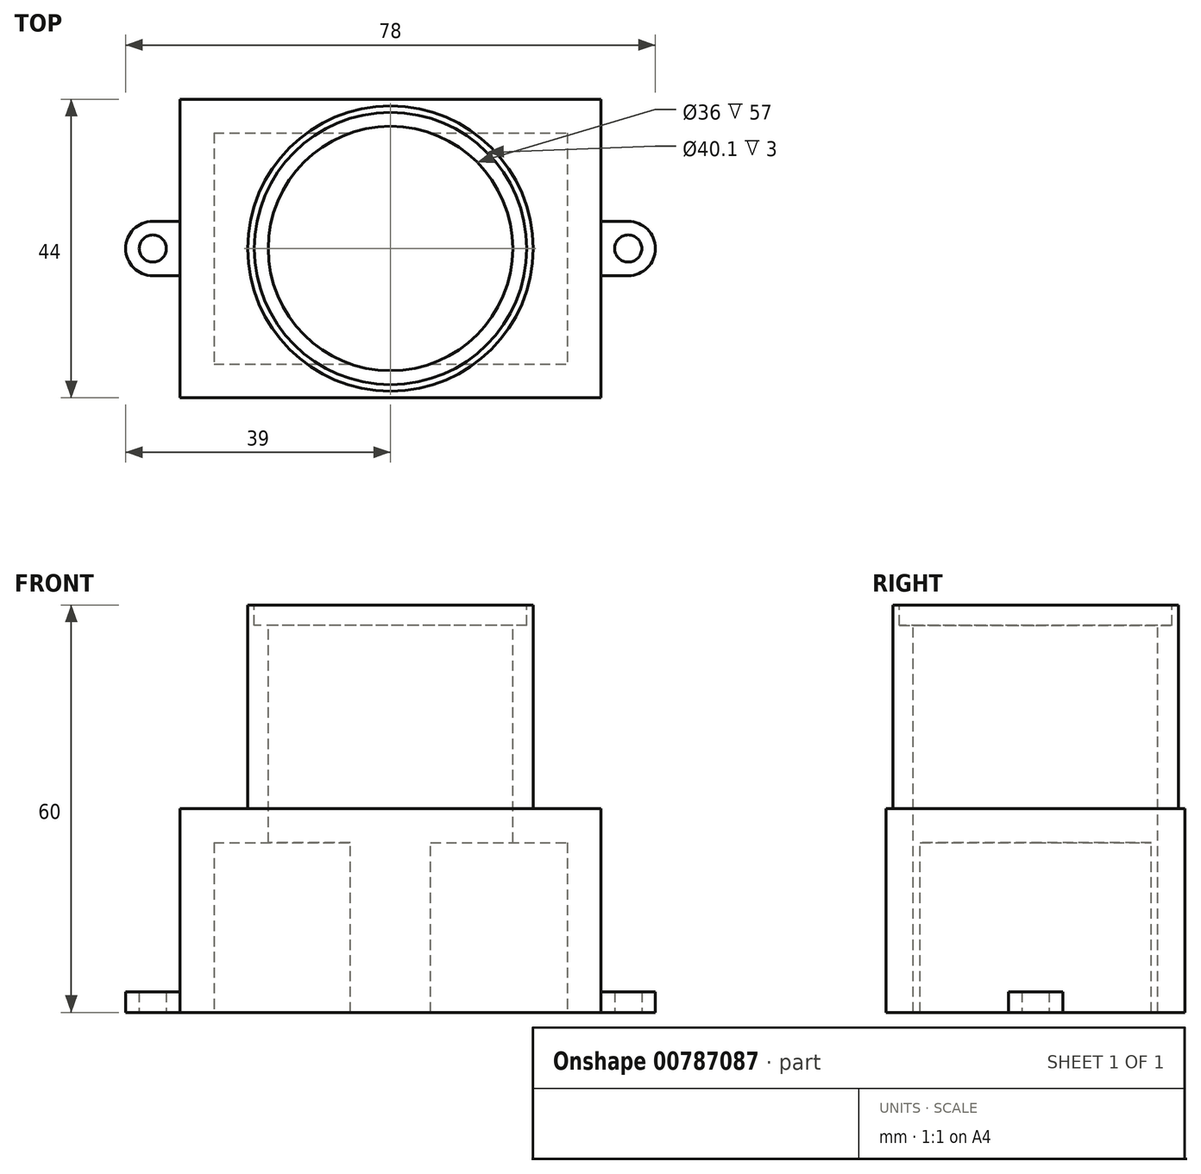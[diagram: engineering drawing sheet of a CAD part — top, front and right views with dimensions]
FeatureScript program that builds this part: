
annotation { "Feature Type Name" : "Feature", "Feature Type Description" : "" }
export const myFeature = defineFeature(function(context is Context, id is Id, definition is map)
    precondition{}
    {
        {
            var Q0;
            Q0=qCreatedBy(makeId("Top.planeOp"),FACE);
            var sketch = newSketch(context, id + "F0", { "sketchPlane" : qUnion([Q0])});
            skLineSegment(sketch, "E0.bottom", {"start": v(-31, 22) * mm, "end": v(31, 22) * mm});
            skLineSegment(sketch, "E0.top", {"start": v(-31, -22) * mm, "end": v(31, -22) * mm});
            skLineSegment(sketch, "E0.left", {"start": v(-31, 22) * mm, "end": v(-31, -22) * mm});
            skLineSegment(sketch, "E0.right", {"start": v(31, 22) * mm, "end": v(31, -22) * mm});
            skPoint(sketch, "E0.middle", {"position": v(0, 0) * mm});
            skSolve(sketch);
        }
        {
            var Q0;
            Q0=makeQuery(id+"F0.imprint","IMPRINT",FACE,{"disambiguationData":[TD([[makeQuery(id+"F0.imprint","IMPRINT",EDGE,{"derivedFrom":sQuery(id+"F0.wireOp",EDGE,"E0.bottom")}),-1.0]])]});
            extrude(context, id + "F1", {"entities" : qUnion([Q0]), "depth" : 30 * mm, "hasSecondDirection" : true, "secondDirectionOppositeDirection" : true, "secondDirectionDepth" : 30 * mm});
        }
        {
            var Q0;
            Q0=makeQuery(id+"F1.opExtrude","CAP_FACE",FACE,{"disambiguationData":[OSD([sQuery(id+"F0.wireOp",EDGE,"E0.bottom"),sQuery(id+"F0.wireOp",EDGE,"E0.top"),sQuery(id+"F0.wireOp",EDGE,"E0.left"),sQuery(id+"F0.wireOp",EDGE,"E0.right")])],"isStart":false});
            var sketch = newSketch(context, id + "F2", { "sketchPlane" : qUnion([Q0])});
            skCircle(sketch, "E1", {"center": v(0, 0) * mm, "radius": 21 * mm});
            skCircle(sketch, "E2", {"center": v(0, 0) * mm, "radius": 18 * mm});
            skSolve(sketch);
        }
        {
            var Q0;
            Q0=makeQuery(id+"F2.imprint","IMPRINT",FACE,{"disambiguationData":[TD([[makeQuery(id+"F2.imprint","IMPRINT",EDGE,{"derivedFrom":sQuery(id+"F2.wireOp",EDGE,"E1")}),-1.0]])]});
            var Q1;
            Q1=makeQuery(id+"F2.imprint","IMPRINT",FACE,{"disambiguationData":[TD([[makeQuery(id+"F2.imprint","IMPRINT",EDGE,{"derivedFrom":sQuery(id+"F2.wireOp",EDGE,"E2")}),1.0]])]});
            var Q2;
            Q2=sQuery(id+"F2.wireOp",EDGE,"E2");
            var Q3;
            Q3=sQuery(id+"F2.wireOp",EDGE,"E1");
            extrude(context, id + "F3", {"entities" : qUnion([Q0, Q1]), "operationType" : NewBodyOperationType.REMOVE, "surfaceEntities" : qUnion([Q2, Q3]), "oppositeDirection" : true, "depth" : 30 * mm});
        }
        {
            var Q0;
            Q0=makeQuery(id+"F1.opExtrude","CAP_FACE",FACE,{"disambiguationData":[OSD([sQuery(id+"F0.wireOp",EDGE,"E0.bottom"),sQuery(id+"F0.wireOp",EDGE,"E0.top"),sQuery(id+"F0.wireOp",EDGE,"E0.left"),sQuery(id+"F0.wireOp",EDGE,"E0.right")])],"isStart":true});
            shell(context, id + "F4", {"entities" : qUnion([Q0]), "thickness" : 5 * mm});
        }
        {
            var Q0;
            Q0=makeQuery(id+"F1.opExtrude","CAP_FACE",FACE,{"disambiguationData":[OSD([sQuery(id+"F0.wireOp",EDGE,"E0.bottom"),sQuery(id+"F0.wireOp",EDGE,"E0.top"),sQuery(id+"F0.wireOp",EDGE,"E0.left"),sQuery(id+"F0.wireOp",EDGE,"E0.right")])],"isStart":true});
            var sketch = newSketch(context, id + "F5", { "sketchPlane" : qUnion([Q0])});
            skLineSegment(sketch, "E3.bottom", {"start": v(31, 4) * mm, "end": v(35, 4) * mm});
            skLineSegment(sketch, "E3.top", {"start": v(31, -4) * mm, "end": v(35, -4) * mm});
            skLineSegment(sketch, "E3.left", {"start": v(31, 4) * mm, "end": v(31, -4) * mm});
            skLineSegment(sketch, "E3.right", {"start": v(39, 0) * mm, "end": v(39, 0) * mm});
            skCircle(sketch, "E4", {"center": v(35, 0) * mm, "radius": 2 * mm});
            skPoint(sketch, "E5.visualSharp", {"position": v(39, 4) * mm});
            skArc(sketch, "E5.filletArc", {"start": v(39, 0) * mm, "mid": v(37.83, 2.83) * mm, "end": v(35, 4) * mm});
            skPoint(sketch, "E6.visualSharp", {"position": v(39, -4) * mm});
            skArc(sketch, "E6.filletArc", {"start": v(35, -4) * mm, "mid": v(37.83, -2.83) * mm, "end": v(39, 0) * mm});
            skCircle(sketch, "E7.MirrorC", {"center": v(-35, 0) * mm, "radius": 2 * mm});
            skPoint(sketch, "E8.MirrorP", {"position": v(-39, 4) * mm});
            skArc(sketch, "E9.MirrorCS", {"start": v(-35, -4) * mm, "mid": v(-37.83, -2.83) * mm, "end": v(-39, 0) * mm});
            skArc(sketch, "E10.MirrorCS", {"start": v(-39, 0) * mm, "mid": v(-37.83, 2.83) * mm, "end": v(-35, 4) * mm});
            skLineSegment(sketch, "E11.MirrorCS", {"start": v(-31, 4) * mm, "end": v(-31, -4) * mm});
            skLineSegment(sketch, "E12.MirrorCS", {"start": v(-31, 4) * mm, "end": v(-35, 4) * mm});
            skLineSegment(sketch, "E13.MirrorCS", {"start": v(-31, -4) * mm, "end": v(-35, -4) * mm});
            skPoint(sketch, "E14.MirrorP", {"position": v(-39, -4) * mm});
            skSolve(sketch);
        }
        {
            var Q0;
            Q0=qSketchRegion(id+"F5",true);
            extrude(context, id + "F6", {"entities" : qUnion([Q0]), "operationType" : NewBodyOperationType.ADD, "oppositeDirection" : true, "depth" : 3 * mm});
        }
        {
            var Q0;
            Q0=makeQuery(id+"F1.opExtrude","CAP_FACE",FACE,{"disambiguationData":[OSD([sQuery(id+"F0.wireOp",EDGE,"E0.bottom"),sQuery(id+"F0.wireOp",EDGE,"E0.top"),sQuery(id+"F0.wireOp",EDGE,"E0.left"),sQuery(id+"F0.wireOp",EDGE,"E0.right")])],"isStart":false});
            var sketch = newSketch(context, id + "F7", { "sketchPlane" : qUnion([Q0])});
            skCircle(sketch, "E15", {"center": v(0, 0) * mm, "radius": 9.05 * mm});
            skSolve(sketch);
        }
        {
            var Q0;
            Q0=qSketchRegion(id+"F7",true);
            extrude(context, id + "F8", {"entities" : qUnion([Q0]), "operationType" : NewBodyOperationType.REMOVE, "oppositeDirection" : true, "depth" : 1.5 * mm});
        }
        {
            var Q0;
            Q0=makeQuery(id+"F3.boolean.opBoolean","COPY",FACE,{"derivedFrom":makeQuery(id+"F3.opExtrude","CAP_FACE",FACE,{"disambiguationData":[OSD([sQuery(id+"F0.wireOp",EDGE,"E0.bottom"),sQuery(id+"F0.wireOp",EDGE,"E0.top"),sQuery(id+"F0.wireOp",EDGE,"E0.left"),sQuery(id+"F0.wireOp",EDGE,"E0.right"),sQuery(id+"F2.wireOp",EDGE,"E1")])],"isStart":false})});
            var sketch = newSketch(context, id + "F9", { "sketchPlane" : qUnion([Q0])});
            skCircle(sketch, "E16", {"center": v(0, 0) * mm, "radius": 18 * mm});
            skSolve(sketch);
        }
        {
            var Q0;
            Q0 = qSketchRegion(id + "F9", true);
            extrude(context, id + "F10", {"entities" : qUnion([Q0]), "operationType" : NewBodyOperationType.REMOVE, "endBound" : BoundingType.THROUGH_ALL, "oppositeDirection" : true, "depth" : 25 * mm, "offsetDistance" : 25 * mm});
        }
        {
            var Q0;
            Q0=makeQuery(id+"F1.opExtrude","CAP_FACE",FACE,{"disambiguationData":[OSD([sQuery(id+"F0.wireOp",EDGE,"E0.bottom"),sQuery(id+"F0.wireOp",EDGE,"E0.top"),sQuery(id+"F0.wireOp",EDGE,"E0.left"),sQuery(id+"F0.wireOp",EDGE,"E0.right")])],"isStart":false});
            var sketch = newSketch(context, id + "F11", { "sketchPlane" : qUnion([Q0])});
            skCircle(sketch, "E17", {"center": v(0, 0) * mm, "radius": 20.05 * mm});
            skSolve(sketch);
        }
        {
            var Q0;
            Q0 = qSketchRegion(id + "F11", true);
            extrude(context, id + "F12", {"entities" : qUnion([Q0]), "operationType" : NewBodyOperationType.REMOVE, "oppositeDirection" : true, "depth" : 3 * mm, "offsetDistance" : 25 * mm});
        }
    });
